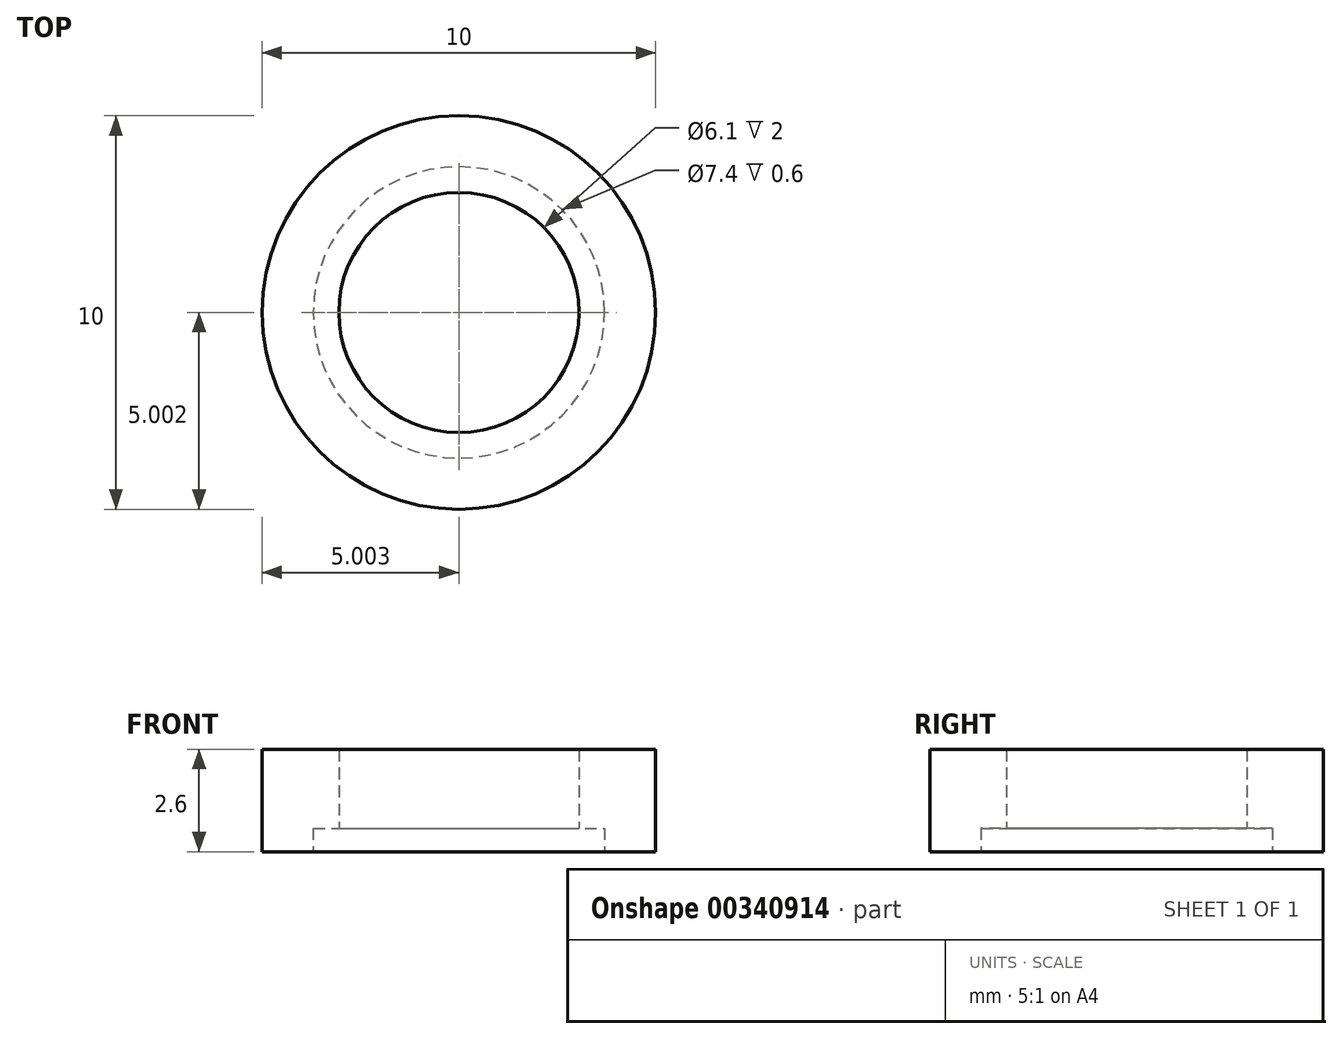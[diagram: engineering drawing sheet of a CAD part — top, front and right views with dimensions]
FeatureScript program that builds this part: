
annotation { "Feature Type Name" : "Feature", "Feature Type Description" : "" }
export const myFeature = defineFeature(function(context is Context, id is Id, definition is map)
    precondition{}
    {
        {
            var Q0;
            Q0=qCreatedBy(makeId("Top.planeOp"),FACE);
            var sketch = newSketch(context, id + "F0", { "sketchPlane" : qUnion([Q0])});
            skCircle(sketch, "E0", {"center": v(-4.42, 6.83) * mm, "radius": 5 * mm});
            skSolve(sketch);
        }
        {
            var Q0;
            Q0 = qSketchRegion(id + "F0", true);
            extrude(context, id + "F1", {"entities" : qUnion([Q0]), "depth" : 2.6 * mm, "offsetDistance" : 25 * mm});
        }
        {
            var Q0;
            Q0=sQuery(id+"F0.wireOp",VERTEX,"E0.center");
            var Q1;
            Q1=makeQuery(id+"F1.opExtrude","SWEPT_BODY",BODY,{"disambiguationData":[OSD([sQuery(id+"F0.wireOp",EDGE,"E0")])]});
            hole(context, id + "F2", {"style" : HoleStyle.C_BORE, "endStyle" : HoleEndStyle.BLIND, "oppositeDirection" : true, "holeDiameter" : 6.1 * mm, "cBoreDiameter" : 7.4 * mm, "cBoreDepth" : 0.6 * mm, "majorDiameter" : 5 * mm, "holeDepth" : 3 * mm, "isTappedThrough" : true, "tappedDepth" : 12 * mm, "tapClearance" : 3, "startFromSketch" : true, "locations" : qUnion([Q0]), "scope" : qUnion([Q1])});
        }
    });
